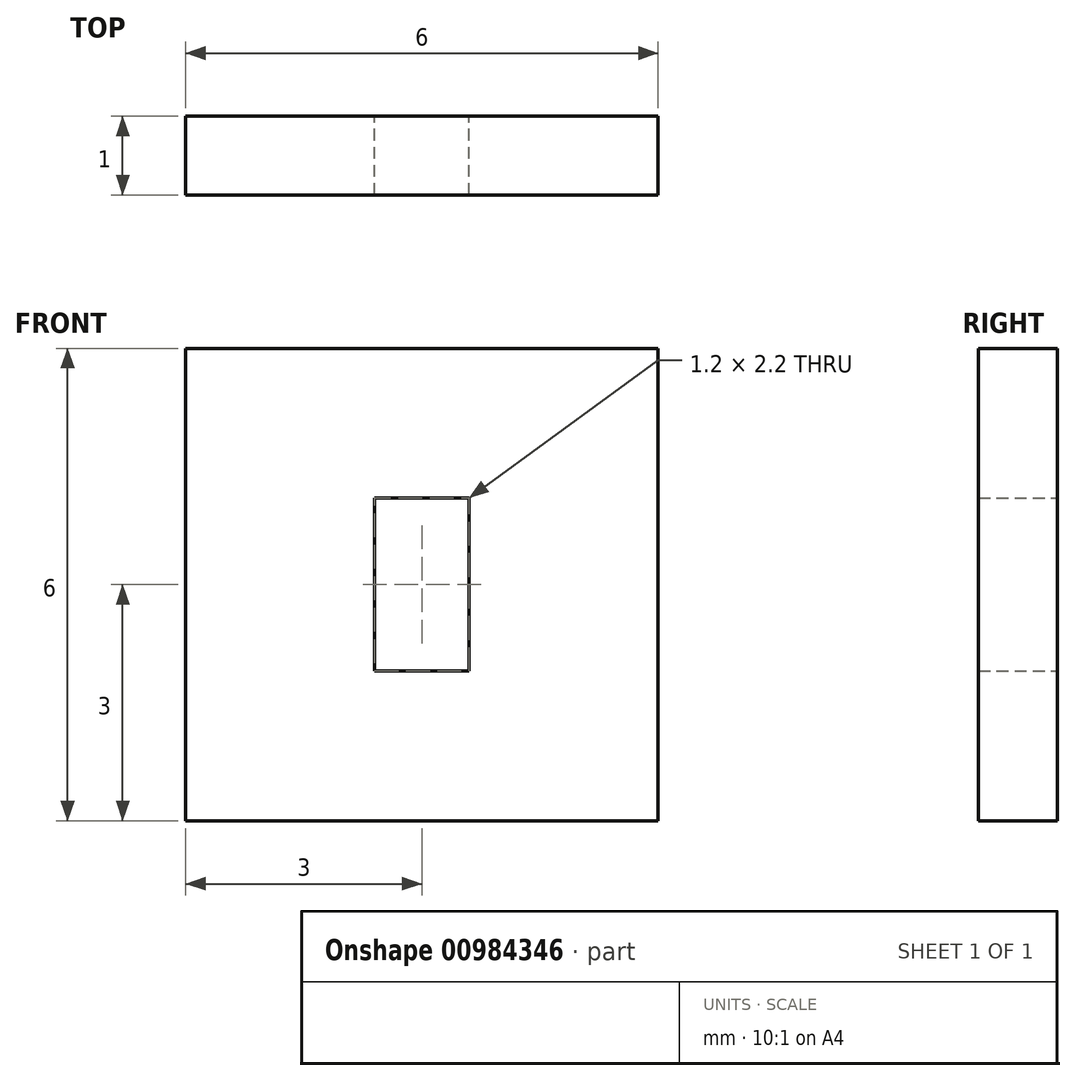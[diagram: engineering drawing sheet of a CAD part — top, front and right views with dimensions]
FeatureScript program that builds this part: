
annotation { "Feature Type Name" : "Feature", "Feature Type Description" : "" }
export const myFeature = defineFeature(function(context is Context, id is Id, definition is map)
    precondition{}
    {
        {
            var Q0;
            Q0=qCreatedBy(makeId("Front.planeOp"),FACE);
            var sketch = newSketch(context, id + "F0", { "sketchPlane" : qUnion([Q0])});
            skLineSegment(sketch, "E0.bottom", {"start": v(3, -3) * mm, "end": v(-3, -3) * mm});
            skLineSegment(sketch, "E0.top", {"start": v(3, 3) * mm, "end": v(-3, 3) * mm});
            skLineSegment(sketch, "E0.left", {"start": v(3, -3) * mm, "end": v(3, 3) * mm});
            skLineSegment(sketch, "E0.right", {"start": v(-3, -3) * mm, "end": v(-3, 3) * mm});
            skPoint(sketch, "E0.middle", {"position": v(0, 0) * mm});
            skLineSegment(sketch, "E1.bottom", {"start": v(0.6, -1.1) * mm, "end": v(-0.6, -1.1) * mm});
            skLineSegment(sketch, "E1.top", {"start": v(0.6, 1.1) * mm, "end": v(-0.6, 1.1) * mm});
            skLineSegment(sketch, "E1.left", {"start": v(0.6, -1.1) * mm, "end": v(0.6, 1.1) * mm});
            skLineSegment(sketch, "E1.right", {"start": v(-0.6, -1.1) * mm, "end": v(-0.6, 1.1) * mm});
            skSolve(sketch);
        }
        {
            var Q0;
            Q0=makeQuery(id+"F0.imprint","IMPRINT",FACE,{"disambiguationData":[TD([[makeQuery(id+"F0.imprint","IMPRINT",EDGE,{"derivedFrom":sQuery(id+"F0.wireOp",EDGE,"E0.bottom")}),-1.0]])]});
            extrude(context, id + "F1", {"entities" : qUnion([Q0]), "depth" : 1 * mm, "offsetDistance" : 25 * mm});
        }
    });
